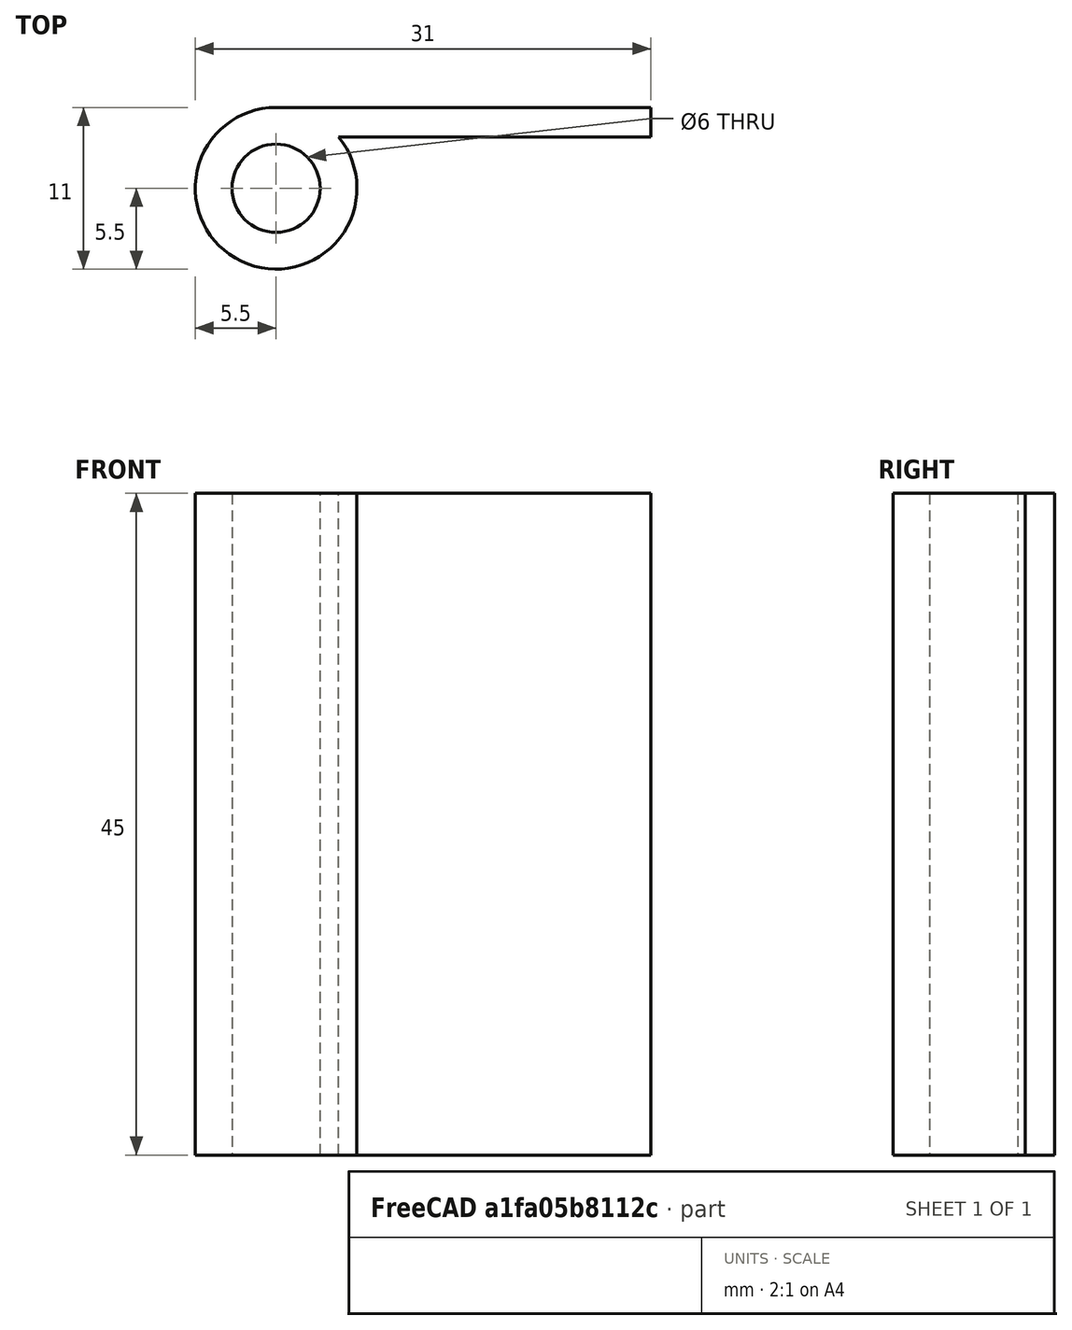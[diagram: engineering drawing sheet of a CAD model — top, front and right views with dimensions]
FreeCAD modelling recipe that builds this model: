
FCSTD DOCUMENT  (FreeCAD 2022.709R28846 (Git))
Label: fischband_fluegel
License: All rights reserved
LicenseURL: http://en.wikipedia.org/wiki/All_rights_reserved
objects: Sketcher::SketchObject×1, PartDesign::Pad×1, PartDesign::Body×1
note: 5 computed .brp shape members not serialized (recipe doc carries the construction recipe); baked Part::Feature solids carry a one-line shape summary decoded from their .brp

FEATURE [Sketcher::SketchObject] Sketch
  ArcFitTolerance = 1e-06
  AttachmentSupport = -> [XY_Plane]
  FullyConstrained = true
  MapMode = 5
  Support = -> [XY_Plane]
  TreeRank = 13
  sketch-geometry (6):
    g0: ArcOfCircle CenterX=0 CenterY=0 CenterZ=0 NormalX=0 NormalY=0 NormalZ=1 AngleXU=0 Radius=5.5 StartAngle=1.5708 EndAngle=6.97296
    g1: Circle CenterX=0 CenterY=0 CenterZ=0 NormalX=0 NormalY=0 NormalZ=1 AngleXU=0 Radius=3
    g2: LineSegment StartX=0 StartY=5.5 StartZ=0 EndX=25.5 EndY=5.5 EndZ=0
    g3: LineSegment StartX=25.5 StartY=5.5 StartZ=0 EndX=25.5 EndY=3.5 EndZ=0
    g4: LineSegment StartX=25.5 StartY=3.5 StartZ=0 EndX=4.24264 EndY=3.5 EndZ=0
    g5: LineSegment [constr] StartX=5.5 StartY=-2.95389e-05 StartZ=0 EndX=5.5 EndY=5.5 EndZ=0
  constraints (18):
    c: Coincident(g0,g-1)
    c: Radius(g0) = 5.5
    c: Coincident(g1,g0)
    c: Radius(g1) = 3
    c: Coincident(g2,g3)
    c: Coincident(g3,g4)
    c: Horizontal(g2)
    c: Horizontal(g4)
    c: Vertical(g3)
    c: Coincident(g0,g2)
    c: Coincident(g0,g4)
    c: DistanceY(g3,g3) = 2
    c: PointOnObject(g0,g-2)
    c: PointOnObject(g5,g0)
    c: PointOnObject(g5,g2)
    c: Vertical(g5)
    c: Tangent(g5,g0)
    c: DistanceX(g5,g2) = 20
FEATURE [PartDesign::Pad] Pad
  ClaimChildren = false
  Direction = (0,0,1)
  Fit = 0
  FitJoin = 0
  InnerFit = 0
  InnerFitJoin = 0
  InnerTaperAngle = 0
  InnerTaperAngleRev = 0
  Length = 45
  Length2 = 100
  Linearize = true
  NewSolid = false
  Profile = -> Sketch
  Suppress = false
  TreeRank = 14
  Type = 0
  _ProfileBasedVersion = 1
FEATURE [PartDesign::Body] Body
  AutoGroupSolids = false
  ClaimAllChildren = false
  ExportMode = 0
  Group = -> [Sketch,Pad]
  Origin = -> Origin
  Tip = -> Pad
  TreeRank = 12
  _ExportChildren = -> [Pad]
  _GroupVersion = 1
